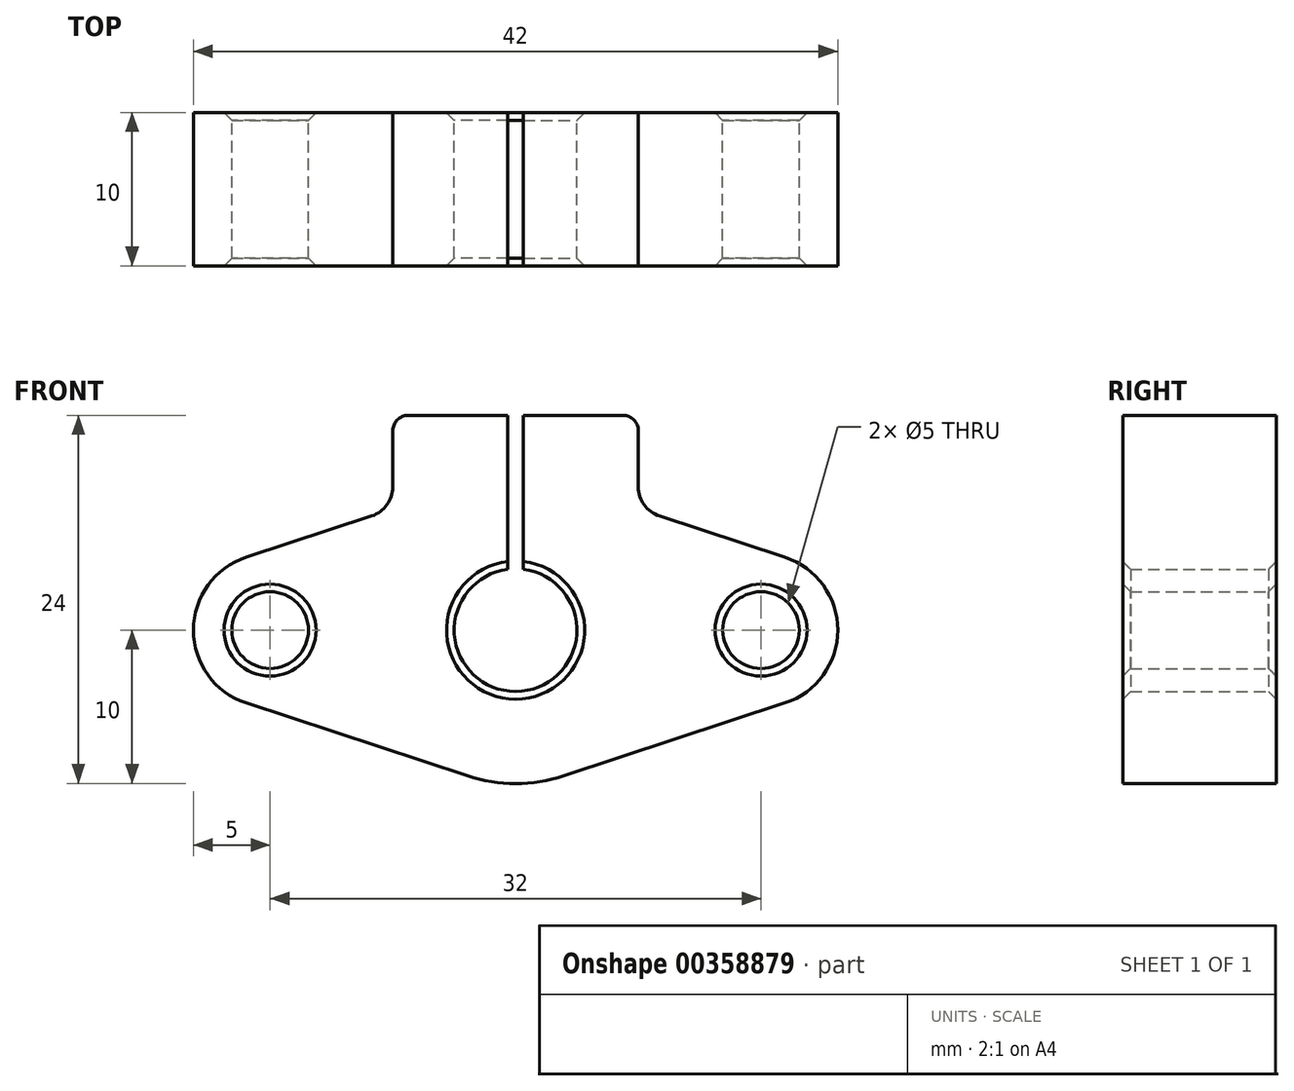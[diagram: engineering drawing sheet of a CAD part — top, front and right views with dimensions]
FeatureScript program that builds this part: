
annotation { "Feature Type Name" : "Feature", "Feature Type Description" : "" }
export const myFeature = defineFeature(function(context is Context, id is Id, definition is map)
    precondition{}
    {
        {
            var Q0;
            Q0=qCreatedBy(makeId("Front.planeOp"),FACE);
            var sketch = newSketch(context, id + "F0", { "sketchPlane" : qUnion([Q0])});
            skCircle(sketch, "E0", {"center": v(0, 0) * mm, "radius": 4 * mm});
            skCircle(sketch, "E1", {"center": v(-16, 0) * mm, "radius": 2.5 * mm});
            skCircle(sketch, "E2", {"center": v(16, 0) * mm, "radius": 2.5 * mm});
            skCircle(sketch, "E3", {"center": v(-16, 0) * mm, "radius": 5 * mm});
            skCircle(sketch, "E4", {"center": v(16, 0) * mm, "radius": 5 * mm});
            skCircle(sketch, "E5", {"center": v(0, 0) * mm, "radius": 10 * mm});
            skLineSegment(sketch, "E6", {"start": v(-17.56, -4.75) * mm, "end": v(-3.12, -9.5) * mm});
            skLineSegment(sketch, "E7", {"start": v(3.12, -9.5) * mm, "end": v(17.56, -4.75) * mm});
            skLineSegment(sketch, "E8", {"start": v(-17.56, 4.75) * mm, "end": v(-9.38, 7.44) * mm});
            skLineSegment(sketch, "E9", {"start": v(9.37, 7.44) * mm, "end": v(17.56, 4.75) * mm});
            skLineSegment(sketch, "E10", {"start": v(-8, 9.34) * mm, "end": v(-8, 13) * mm});
            skLineSegment(sketch, "E11", {"start": v(-7, 14) * mm, "end": v(7, 14) * mm});
            skLineSegment(sketch, "E12", {"start": v(8, 13) * mm, "end": v(8, 9.34) * mm});
            skPoint(sketch, "E13.newPointB", {"position": v(-8, 0) * mm});
            skArc(sketch, "E13.filletArc", {"start": v(-9.38, 7.44) * mm, "mid": v(-8.38, 8.17) * mm, "end": v(-8, 9.34) * mm});
            skPoint(sketch, "E14.visualSharp", {"position": v(-8, 14) * mm});
            skArc(sketch, "E14.filletArc", {"start": v(-7, 14) * mm, "mid": v(-7.7, 13.7) * mm, "end": v(-8, 13) * mm});
            skPoint(sketch, "E15.visualSharp", {"position": v(8, 14) * mm});
            skArc(sketch, "E15.filletArc", {"start": v(8, 13) * mm, "mid": v(7.7, 13.7) * mm, "end": v(7, 14) * mm});
            skPoint(sketch, "E16.newPointA", {"position": v(8, 0) * mm});
            skArc(sketch, "E16.filletArc", {"start": v(8, 9.34) * mm, "mid": v(8.38, 8.17) * mm, "end": v(9.37, 7.44) * mm});
            skLineSegment(sketch, "E17", {"start": v(-0.5, 0) * mm, "end": v(-0.5, 14) * mm});
            skLineSegment(sketch, "E18", {"start": v(0.5, 0) * mm, "end": v(0.5, 14) * mm});
            skSolve(sketch);
        }
        {
            var Q0;
            {var subQ0=sQuery(id+"F0.wireOp",EDGE,"E9");Q0=makeQuery(id+"F0.imprint","IMPRINT",FACE,{"disambiguationData":[TD([[makeQuery(id+"F0.imprint","IMPRINT",EDGE,{"derivedFrom":subQ0}),-1.0]])]});}
            var Q1;
            {var subQ0=sQuery(id+"F0.wireOp",EDGE,"E5");var subQ1=sQuery(id+"F0.wireOp",EDGE,"E4");var subQ2=makeQuery(id+"F0.imprint","INTERSECT",VERTEX,{"disambiguationData":[OD(0.0)],"derivedFrom":[subQ1,subQ0]});Q1=makeQuery(id+"F0.imprint","IMPRINT",FACE,{"disambiguationData":[TD([[makeQuery(id+"F0.imprint","IMPRINT",EDGE,{"disambiguationData":[TD([[subQ2,-1.0]])],"derivedFrom":subQ1}),1.0]])]});}
            var Q2;
            Q2=makeQuery(id+"F0.imprint","IMPRINT",FACE,{"disambiguationData":[TD([[makeQuery(id+"F0.imprint","IMPRINT",EDGE,{"derivedFrom":sQuery(id+"F0.wireOp",EDGE,"E2")}),-1.0]])]});
            var Q3;
            {var subQ0=sQuery(id+"F0.wireOp",EDGE,"E7");Q3=makeQuery(id+"F0.imprint","IMPRINT",FACE,{"disambiguationData":[TD([[makeQuery(id+"F0.imprint","IMPRINT",EDGE,{"derivedFrom":subQ0}),1.0]])]});}
            var Q4;
            {var subQ0=sQuery(id+"F0.wireOp",EDGE,"E5");var subQ1=sQuery(id+"F0.wireOp",EDGE,"E3");var subQ2=makeQuery(id+"F0.imprint","INTERSECT",VERTEX,{"disambiguationData":[OD(0.0)],"derivedFrom":[subQ1,subQ0]});Q4=makeQuery(id+"F0.imprint","IMPRINT",FACE,{"disambiguationData":[TD([[makeQuery(id+"F0.imprint","IMPRINT",EDGE,{"disambiguationData":[TD([[subQ2,1.0]])],"derivedFrom":subQ1}),1.0]])]});}
            var Q5;
            {var subQ0=sQuery(id+"F0.wireOp",EDGE,"E8");Q5=makeQuery(id+"F0.imprint","IMPRINT",FACE,{"disambiguationData":[TD([[makeQuery(id+"F0.imprint","IMPRINT",EDGE,{"derivedFrom":subQ0}),-1.0]])]});}
            var Q6;
            {var subQ0=sQuery(id+"F0.wireOp",EDGE,"E6");var subQ1=sQuery(id+"F0.wireOp",EDGE,"E3");var subQ2=makeQuery(id+"F0.imprint","INTERSECT",VERTEX,{"derivedFrom":[subQ1,subQ0]});Q6=makeQuery(id+"F0.imprint","IMPRINT",FACE,{"disambiguationData":[TD([[makeQuery(id+"F0.imprint","IMPRINT",EDGE,{"disambiguationData":[TD([[subQ2,-1.0]])],"derivedFrom":subQ1}),-1.0]])]});}
            var Q7;
            Q7=makeQuery(id+"F0.imprint","IMPRINT",FACE,{"disambiguationData":[TD([[makeQuery(id+"F0.imprint","IMPRINT",EDGE,{"derivedFrom":sQuery(id+"F0.wireOp",EDGE,"E1")}),-1.0]])]});
            var Q8;
            {var subQ5=sQuery(id+"F0.wireOp",EDGE,"E17");var subQ7=sQuery(id+"F0.wireOp",EDGE,"E0");var subQ8=makeQuery(id+"F0.imprint","INTERSECT",VERTEX,{"derivedFrom":[subQ7,subQ5]});Q8=makeQuery(id+"F0.imprint","IMPRINT",FACE,{"disambiguationData":[TD([[makeQuery(id+"F0.imprint","IMPRINT",EDGE,{"disambiguationData":[TD([[subQ8,-1.0]])],"derivedFrom":subQ7}),-1.0]])]});}
            extrude(context, id + "F1", {"entities" : qUnion([Q0, Q1, Q2, Q3, Q4, Q5, Q6, Q7, Q8]), "depth" : 10 * mm});
        }
        {
            var Q0;
            Q0=makeQuery(id+"F1.opExtrude","CAP_EDGE",EDGE,{"disambiguationData":[OSD([sQuery(id+"F0.wireOp",EDGE,"E1")])],"isStart":false});
            var Q1;
            Q1=makeQuery(id+"F1.opExtrude","CAP_EDGE",EDGE,{"disambiguationData":[OSD([sQuery(id+"F0.wireOp",EDGE,"E0")])],"isStart":false});
            var Q2;
            Q2=makeQuery(id+"F1.opExtrude","CAP_EDGE",EDGE,{"disambiguationData":[OSD([sQuery(id+"F0.wireOp",EDGE,"E2")])],"isStart":false});
            var Q3;
            Q3=makeQuery(id+"F1.opExtrude","CAP_EDGE",EDGE,{"disambiguationData":[OSD([sQuery(id+"F0.wireOp",EDGE,"E2")])],"isStart":true});
            var Q4;
            Q4=makeQuery(id+"F1.opExtrude","CAP_EDGE",EDGE,{"disambiguationData":[OSD([sQuery(id+"F0.wireOp",EDGE,"E0")])],"isStart":true});
            var Q5;
            Q5=makeQuery(id+"F1.opExtrude","CAP_EDGE",EDGE,{"disambiguationData":[OSD([sQuery(id+"F0.wireOp",EDGE,"E1")])],"isStart":true});
            chamfer(context, id + "F2", {"entities" : qUnion([Q0, Q1, Q2, Q3, Q4, Q5]), "width" : 0.5 * mm, "tangentPropagation" : true});
        }
    });
